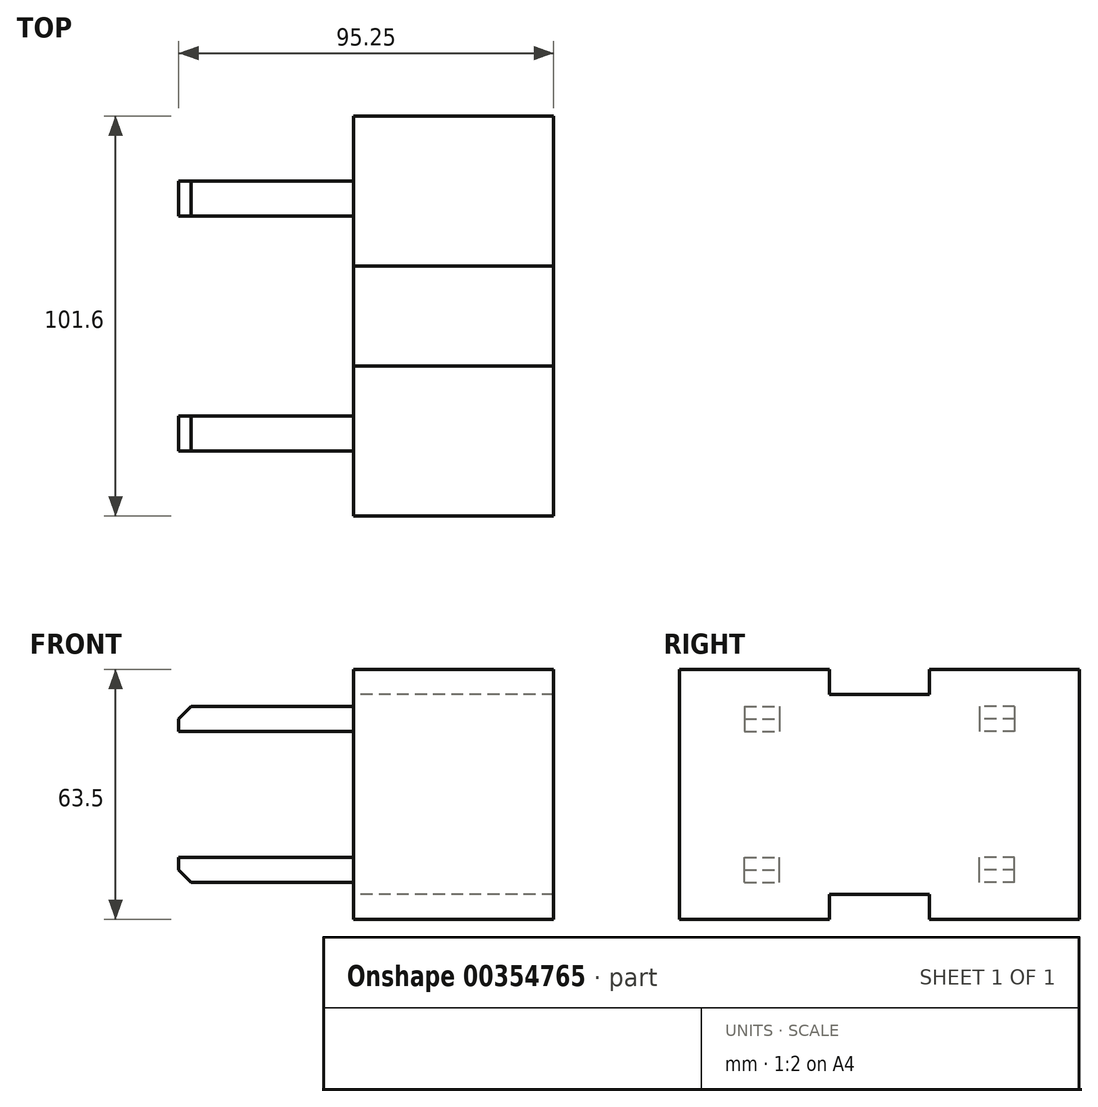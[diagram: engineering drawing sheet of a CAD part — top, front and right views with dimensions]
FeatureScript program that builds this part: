
annotation { "Feature Type Name" : "Feature", "Feature Type Description" : "" }
export const myFeature = defineFeature(function(context is Context, id is Id, definition is map)
    precondition{}
    {
        {
            var Q0;
            Q0=qCreatedBy(makeId("Right.planeOp"),FACE);
            var sketch = newSketch(context, id + "F0", { "sketchPlane" : qUnion([Q0])});
            skLineSegment(sketch, "E0", {"start": v(0, 25.4) * mm, "end": v(-12.7, 25.4) * mm});
            skLineSegment(sketch, "E1", {"start": v(-12.7, 25.4) * mm, "end": v(-12.7, 31.75) * mm});
            skLineSegment(sketch, "E2", {"start": v(-12.7, 31.75) * mm, "end": v(-50.8, 31.75) * mm});
            skLineSegment(sketch, "E3", {"start": v(-50.8, 31.75) * mm, "end": v(-50.8, 0) * mm});
            skLineSegment(sketch, "E4.MirrorCS", {"start": v(-50.8, -31.75) * mm, "end": v(-50.8, 0) * mm});
            skLineSegment(sketch, "E5.MirrorCS", {"start": v(-12.7, -31.75) * mm, "end": v(-50.8, -31.75) * mm});
            skLineSegment(sketch, "E6.MirrorCS", {"start": v(-12.7, -25.4) * mm, "end": v(-12.7, -31.75) * mm});
            skLineSegment(sketch, "E7.MirrorCS", {"start": v(0, -25.4) * mm, "end": v(-12.7, -25.4) * mm});
            skLineSegment(sketch, "E8.MirrorCS", {"start": v(0, 25.4) * mm, "end": v(12.7, 25.4) * mm});
            skLineSegment(sketch, "E9.MirrorCS", {"start": v(12.7, 25.4) * mm, "end": v(12.7, 31.75) * mm});
            skLineSegment(sketch, "E10.MirrorCS", {"start": v(0, -25.4) * mm, "end": v(12.7, -25.4) * mm});
            skLineSegment(sketch, "E11.MirrorCS", {"start": v(12.7, -25.4) * mm, "end": v(12.7, -31.75) * mm});
            skLineSegment(sketch, "E12.MirrorCS", {"start": v(12.7, 31.75) * mm, "end": v(50.8, 31.75) * mm});
            skLineSegment(sketch, "E13.MirrorCS", {"start": v(50.8, -31.75) * mm, "end": v(50.8, 0) * mm});
            skLineSegment(sketch, "E14.MirrorCS", {"start": v(12.7, -31.75) * mm, "end": v(50.8, -31.75) * mm});
            skLineSegment(sketch, "E15.MirrorCS", {"start": v(50.8, 31.75) * mm, "end": v(50.8, 0) * mm});
            skSolve(sketch);
        }
        {
            var Q0;
            Q0=makeQuery(id+"F0.imprint","IMPRINT",FACE,{"disambiguationData":[TD([[makeQuery(id+"F0.imprint","IMPRINT",EDGE,{"derivedFrom":sQuery(id+"F0.wireOp",EDGE,"E0")}),1.0]])]});
            extrude(context, id + "F1", {"entities" : qUnion([Q0]), "depth" : 50.8 * mm});
        }
        {
            var Q0;
            Q0=qCreatedBy(makeId("Front.planeOp"),FACE);
            var sketch = newSketch(context, id + "F2", { "sketchPlane" : qUnion([Q0])});
            skLineSegment(sketch, "E16", {"start": v(0, 25.4) * mm, "end": v(-41.28, 25.4) * mm});
            skLineSegment(sketch, "E17", {"start": v(-41.28, 25.4) * mm, "end": v(-44.45, 22.23) * mm});
            skLineSegment(sketch, "E18", {"start": v(-44.45, 22.22) * mm, "end": v(-44.45, 19.05) * mm});
            skLineSegment(sketch, "E19", {"start": v(-44.45, 19.05) * mm, "end": v(0, 19.05) * mm});
            skLineSegment(sketch, "E20", {"start": v(0, 25.4) * mm, "end": v(0, 19.05) * mm});
            skSolve(sketch);
        }
        {
            var Q0;
            Q0=makeQuery(id+"F2.imprint","IMPRINT",FACE,{"disambiguationData":[TD([[makeQuery(id+"F2.imprint","IMPRINT",EDGE,{"derivedFrom":sQuery(id+"F2.wireOp",EDGE,"E16")}),1.0]])]});
            extrude(context, id + "F3", {"entities" : qUnion([Q0]), "depth" : 8.9 * mm});
        }
        {
            var Q0;
            Q0=makeQuery(id+"F3.opExtrude","SWEPT_BODY",BODY,{"disambiguationData":[OSD([sQuery(id+"F2.wireOp",EDGE,"E16"),sQuery(id+"F2.wireOp",EDGE,"E17"),sQuery(id+"F2.wireOp",EDGE,"E18"),sQuery(id+"F2.wireOp",EDGE,"E19"),sQuery(id+"F2.wireOp",EDGE,"E20")])]});
            var Q1;
            Q1=qCreatedBy(makeId("Top.planeOp"),FACE);
            mirror(context, id + "F4", {"entities" : qUnion([Q0]), "mirrorPlane" : qUnion([Q1])});
        }
        {
            var Q0;
            Q0=makeQuery(id+"F3.opExtrude","SWEPT_BODY",BODY,{"disambiguationData":[OSD([sQuery(id+"F2.wireOp",EDGE,"E16"),sQuery(id+"F2.wireOp",EDGE,"E17"),sQuery(id+"F2.wireOp",EDGE,"E18"),sQuery(id+"F2.wireOp",EDGE,"E19"),sQuery(id+"F2.wireOp",EDGE,"E20")])]});
            var Q1;
            Q1=makeQuery(id+"F4.opPattern","COPY",BODY,{"derivedFrom":makeQuery(id+"F3.opExtrude","SWEPT_BODY",BODY,{"disambiguationData":[OSD([sQuery(id+"F2.wireOp",EDGE,"E16"),sQuery(id+"F2.wireOp",EDGE,"E17"),sQuery(id+"F2.wireOp",EDGE,"E18"),sQuery(id+"F2.wireOp",EDGE,"E19"),sQuery(id+"F2.wireOp",EDGE,"E20")])]}),"instanceName":"1"});
            var Q2;
            Q2=makeQuery(id+"F1.opExtrude","CAP_EDGE",EDGE,{"disambiguationData":[OSD([sQuery(id+"F0.wireOp",EDGE,"E2")])],"isStart":true});
            transform(context, id + "F5", {"entities" : qUnion([Q0, Q1]), "transformType" : TransformType.TRANSLATION_ENTITY, "oppositeDirectionEntity" : false, "transformLine" : qUnion([Q2]), "makeCopy" : false});
        }
        {
            var Q0;
            Q0=makeQuery(id+"F3.opExtrude","SWEPT_BODY",BODY,{"disambiguationData":[OSD([sQuery(id+"F2.wireOp",EDGE,"E16"),sQuery(id+"F2.wireOp",EDGE,"E17"),sQuery(id+"F2.wireOp",EDGE,"E18"),sQuery(id+"F2.wireOp",EDGE,"E19"),sQuery(id+"F2.wireOp",EDGE,"E20")])]});
            transform(context, id + "F6", {"entities" : qUnion([Q0]), "transformType" : TransformType.TRANSLATION_3D, "dx" : 0 * mm, "dy" : 0 * mm, "dz" : 5.08 * mm, "makeCopy" : false});
        }
        {
            var Q0;
            Q0=makeQuery(id+"F4.opPattern","COPY",BODY,{"derivedFrom":makeQuery(id+"F3.opExtrude","SWEPT_BODY",BODY,{"disambiguationData":[OSD([sQuery(id+"F2.wireOp",EDGE,"E16"),sQuery(id+"F2.wireOp",EDGE,"E17"),sQuery(id+"F2.wireOp",EDGE,"E18"),sQuery(id+"F2.wireOp",EDGE,"E19"),sQuery(id+"F2.wireOp",EDGE,"E20")])]}),"instanceName":"1"});
            transform(context, id + "F7", {"entities" : qUnion([Q0]), "transformType" : TransformType.TRANSLATION_3D, "dx" : 0 * mm, "dy" : 0 * mm, "dz" : -5.08 * mm, "makeCopy" : false});
        }
        {
            var Q0;
            Q0=makeQuery(id+"F3.opExtrude","SWEPT_BODY",BODY,{"disambiguationData":[OSD([sQuery(id+"F2.wireOp",EDGE,"E16"),sQuery(id+"F2.wireOp",EDGE,"E17"),sQuery(id+"F2.wireOp",EDGE,"E18"),sQuery(id+"F2.wireOp",EDGE,"E19"),sQuery(id+"F2.wireOp",EDGE,"E20")])]});
            var Q1;
            Q1=makeQuery(id+"F4.opPattern","COPY",BODY,{"derivedFrom":makeQuery(id+"F3.opExtrude","SWEPT_BODY",BODY,{"disambiguationData":[OSD([sQuery(id+"F2.wireOp",EDGE,"E16"),sQuery(id+"F2.wireOp",EDGE,"E17"),sQuery(id+"F2.wireOp",EDGE,"E18"),sQuery(id+"F2.wireOp",EDGE,"E19"),sQuery(id+"F2.wireOp",EDGE,"E20")])]}),"instanceName":"1"});
            var Q2;
            Q2=qCreatedBy(makeId("Front.planeOp"),FACE);
            mirror(context, id + "F8", {"entities" : qUnion([Q0, Q1]), "mirrorPlane" : qUnion([Q2])});
        }
        {
            var Q0;
            Q0=makeQuery(id+"F3.opExtrude","SWEPT_BODY",BODY,{"disambiguationData":[OSD([sQuery(id+"F2.wireOp",EDGE,"E16"),sQuery(id+"F2.wireOp",EDGE,"E17"),sQuery(id+"F2.wireOp",EDGE,"E18"),sQuery(id+"F2.wireOp",EDGE,"E19"),sQuery(id+"F2.wireOp",EDGE,"E20")])]});
            transform(context, id + "F9", {"entities" : qUnion([Q0]), "transformType" : TransformType.TRANSLATION_3D, "dx" : 0 * mm, "dy" : 0 * mm, "dz" : -8.13 * mm, "makeCopy" : false});
        }
        {
            var Q0;
            Q0=makeQuery(id+"F8.opPattern","COPY",BODY,{"derivedFrom":makeQuery(id+"F3.opExtrude","SWEPT_BODY",BODY,{"disambiguationData":[OSD([sQuery(id+"F2.wireOp",EDGE,"E16"),sQuery(id+"F2.wireOp",EDGE,"E17"),sQuery(id+"F2.wireOp",EDGE,"E18"),sQuery(id+"F2.wireOp",EDGE,"E19"),sQuery(id+"F2.wireOp",EDGE,"E20")])]}),"instanceName":"1"});
            transform(context, id + "F10", {"entities" : qUnion([Q0]), "transformType" : TransformType.TRANSLATION_3D, "dx" : 0 * mm, "dy" : 0 * mm, "dz" : -8.13 * mm, "makeCopy" : false});
        }
        {
            var Q0;
            Q0=makeQuery(id+"F8.opPattern","COPY",BODY,{"derivedFrom":makeQuery(id+"F4.opPattern","COPY",BODY,{"derivedFrom":makeQuery(id+"F3.opExtrude","SWEPT_BODY",BODY,{"disambiguationData":[OSD([sQuery(id+"F2.wireOp",EDGE,"E16"),sQuery(id+"F2.wireOp",EDGE,"E17"),sQuery(id+"F2.wireOp",EDGE,"E18"),sQuery(id+"F2.wireOp",EDGE,"E19"),sQuery(id+"F2.wireOp",EDGE,"E20")])]}),"instanceName":"1"}),"instanceName":"1"});
            var Q1;
            Q1=makeQuery(id+"F4.opPattern","COPY",BODY,{"derivedFrom":makeQuery(id+"F3.opExtrude","SWEPT_BODY",BODY,{"disambiguationData":[OSD([sQuery(id+"F2.wireOp",EDGE,"E16"),sQuery(id+"F2.wireOp",EDGE,"E17"),sQuery(id+"F2.wireOp",EDGE,"E18"),sQuery(id+"F2.wireOp",EDGE,"E19"),sQuery(id+"F2.wireOp",EDGE,"E20")])]}),"instanceName":"1"});
            transform(context, id + "F11", {"entities" : qUnion([Q0, Q1]), "transformType" : TransformType.TRANSLATION_3D, "dx" : 0 * mm, "dy" : 0 * mm, "dz" : 8.13 * mm, "makeCopy" : false});
        }
        {
            var Q0;
            Q0=makeQuery(id+"F3.opExtrude","SWEPT_BODY",BODY,{"disambiguationData":[OSD([sQuery(id+"F2.wireOp",EDGE,"E16"),sQuery(id+"F2.wireOp",EDGE,"E17"),sQuery(id+"F2.wireOp",EDGE,"E18"),sQuery(id+"F2.wireOp",EDGE,"E19"),sQuery(id+"F2.wireOp",EDGE,"E20")])]});
            var Q1;
            Q1=makeQuery(id+"F4.opPattern","COPY",BODY,{"derivedFrom":makeQuery(id+"F3.opExtrude","SWEPT_BODY",BODY,{"disambiguationData":[OSD([sQuery(id+"F2.wireOp",EDGE,"E16"),sQuery(id+"F2.wireOp",EDGE,"E17"),sQuery(id+"F2.wireOp",EDGE,"E18"),sQuery(id+"F2.wireOp",EDGE,"E19"),sQuery(id+"F2.wireOp",EDGE,"E20")])]}),"instanceName":"1"});
            transform(context, id + "F12", {"entities" : qUnion([Q0, Q1]), "transformType" : TransformType.TRANSLATION_3D, "dx" : 0 * mm, "dy" : 12.7 * mm, "dz" : 0 * mm, "makeCopy" : false});
        }
        {
            var Q0;
            Q0=makeQuery(id+"F8.opPattern","COPY",BODY,{"derivedFrom":makeQuery(id+"F3.opExtrude","SWEPT_BODY",BODY,{"disambiguationData":[OSD([sQuery(id+"F2.wireOp",EDGE,"E16"),sQuery(id+"F2.wireOp",EDGE,"E17"),sQuery(id+"F2.wireOp",EDGE,"E18"),sQuery(id+"F2.wireOp",EDGE,"E19"),sQuery(id+"F2.wireOp",EDGE,"E20")])]}),"instanceName":"1"});
            var Q1;
            Q1=makeQuery(id+"F8.opPattern","COPY",BODY,{"derivedFrom":makeQuery(id+"F4.opPattern","COPY",BODY,{"derivedFrom":makeQuery(id+"F3.opExtrude","SWEPT_BODY",BODY,{"disambiguationData":[OSD([sQuery(id+"F2.wireOp",EDGE,"E16"),sQuery(id+"F2.wireOp",EDGE,"E17"),sQuery(id+"F2.wireOp",EDGE,"E18"),sQuery(id+"F2.wireOp",EDGE,"E19"),sQuery(id+"F2.wireOp",EDGE,"E20")])]}),"instanceName":"1"}),"instanceName":"1"});
            transform(context, id + "F13", {"entities" : qUnion([Q0, Q1]), "transformType" : TransformType.TRANSLATION_3D, "dx" : 0 * mm, "dy" : -12.7 * mm, "dz" : 0 * mm, "makeCopy" : false});
        }
    });
